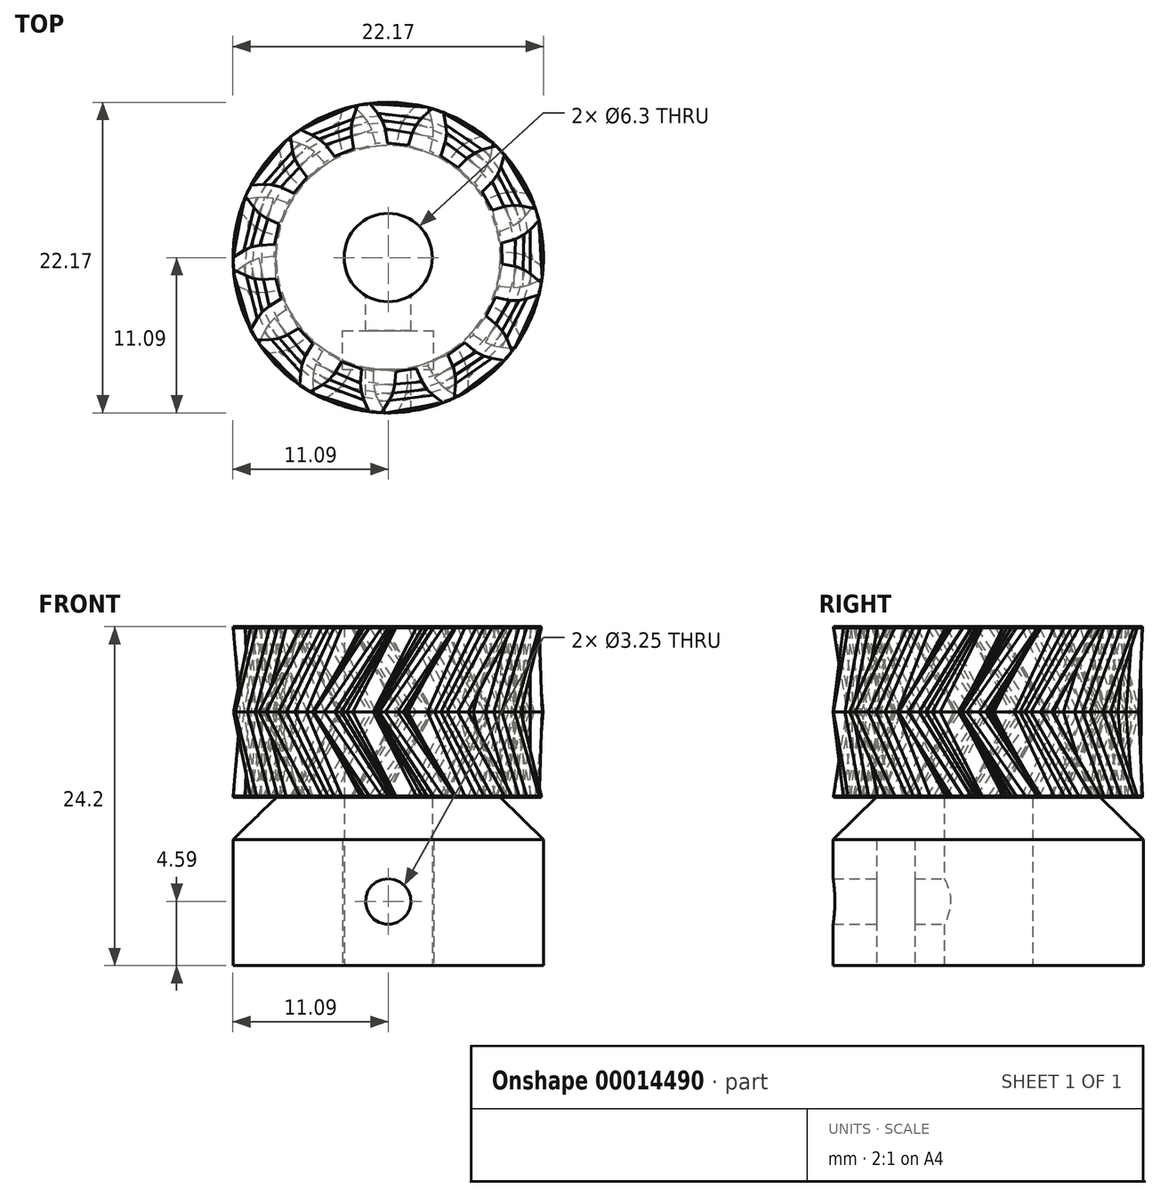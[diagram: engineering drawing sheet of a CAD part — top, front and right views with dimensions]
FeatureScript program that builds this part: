
annotation { "Feature Type Name" : "Feature", "Feature Type Description" : "" }
export const myFeature = defineFeature(function(context is Context, id is Id, definition is map)
    precondition{}
    {
        {
            var Q0;
            Q0=qCreatedBy(makeId("Top.planeOp"),FACE);
            cPlane(context, id + "F0", {"entities" : qUnion([Q0]), "cplaneType" : CPlaneType.OFFSET, "offset" : 6 * mm, "width" : 150 * mm, "height" : 150 * mm});
        }
        {
            var Q0;
            Q0=qCreatedBy(makeId("Top.planeOp"),FACE);
            var sketch = newSketch(context, id + "F1", { "sketchPlane" : qUnion([Q0])});
            skLineSegment(sketch, "E0", {"start": v(-2.62, 9.44) * mm, "end": v(-2.49, 10) * mm});
            skLineSegment(sketch, "E1", {"start": v(-2.49, 10) * mm, "end": v(-2.18, 10.87) * mm});
            skLineSegment(sketch, "E2", {"start": v(-1.33, 11) * mm, "end": v(-2.18, 10.87) * mm});
            skPoint(sketch, "E3.center", {"position": v(0, 0) * mm});
            skLineSegment(sketch, "E4", {"start": v(-1.76, 10.94) * mm, "end": v(-1.26, 7.98) * mm, "construction": true});
            skLineSegment(sketch, "E5", {"start": v(-2.47, 7.78) * mm, "end": v(-2.64, 8.79) * mm});
            skLineSegment(sketch, "E6", {"start": v(-2.64, 8.79) * mm, "end": v(-2.62, 9.44) * mm});
            skLineSegment(sketch, "E7.MirrorCS", {"start": v(-0.05, 8.18) * mm, "end": v(-0.22, 9.2) * mm});
            skLineSegment(sketch, "E8.MirrorCS", {"start": v(-0.22, 9.2) * mm, "end": v(-0.45, 9.8) * mm});
            skLineSegment(sketch, "E9.MirrorCS", {"start": v(-0.76, 10.3) * mm, "end": v(-1.33, 11) * mm});
            skLineSegment(sketch, "E10.MirrorCS", {"start": v(-0.45, 9.8) * mm, "end": v(-0.76, 10.3) * mm});
            skLineSegment(sketch, "E11", {"start": v(-0.05, 8.18) * mm, "end": v(1.43, 8.03) * mm});
            skLineSegment(sketch, "E12.1.0", {"start": v(-6.7, 7.14) * mm, "end": v(-6.85, 7.7) * mm});
            skLineSegment(sketch, "E12.1.1", {"start": v(-5.45, 8.76) * mm, "end": v(-6.3, 9.13) * mm});
            skLineSegment(sketch, "E12.1.2", {"start": v(-6.3, 9.13) * mm, "end": v(-6.98, 8.6) * mm});
            skLineSegment(sketch, "E12.1.3", {"start": v(-6.85, 7.7) * mm, "end": v(-6.98, 8.6) * mm});
            skLineSegment(sketch, "E12.1.4", {"start": v(-5.8, 5.74) * mm, "end": v(-6.42, 6.55) * mm});
            skLineSegment(sketch, "E12.1.5", {"start": v(-4.47, 8.04) * mm, "end": v(-4.96, 8.47) * mm});
            skLineSegment(sketch, "E12.1.6", {"start": v(-3.85, 7.22) * mm, "end": v(-2.47, 7.78) * mm});
            skLineSegment(sketch, "E12.1.7", {"start": v(-4.96, 8.47) * mm, "end": v(-5.45, 8.76) * mm});
            skLineSegment(sketch, "E12.1.8", {"start": v(-6.42, 6.55) * mm, "end": v(-6.7, 7.14) * mm});
            skLineSegment(sketch, "E12.1.9", {"start": v(-3.85, 7.22) * mm, "end": v(-4.47, 8.04) * mm});
            skLineSegment(sketch, "E12.2.0", {"start": v(-9.26, 3.2) * mm, "end": v(-9.64, 3.63) * mm});
            skLineSegment(sketch, "E12.2.1", {"start": v(-8.9, 5.22) * mm, "end": v(-9.81, 5.16) * mm});
            skLineSegment(sketch, "E12.2.2", {"start": v(-9.81, 5.16) * mm, "end": v(-10.18, 4.38) * mm});
            skLineSegment(sketch, "E12.2.3", {"start": v(-9.64, 3.63) * mm, "end": v(-10.18, 4.38) * mm});
            skLineSegment(sketch, "E12.2.4", {"start": v(-7.8, 2.39) * mm, "end": v(-8.73, 2.82) * mm});
            skLineSegment(sketch, "E12.2.5", {"start": v(-7.69, 5.04) * mm, "end": v(-8.33, 5.2) * mm});
            skLineSegment(sketch, "E12.2.6", {"start": v(-6.76, 4.6) * mm, "end": v(-5.8, 5.74) * mm});
            skLineSegment(sketch, "E12.2.7", {"start": v(-8.33, 5.2) * mm, "end": v(-8.9, 5.22) * mm});
            skLineSegment(sketch, "E12.2.8", {"start": v(-8.73, 2.82) * mm, "end": v(-9.26, 3.2) * mm});
            skLineSegment(sketch, "E12.2.9", {"start": v(-6.76, 4.6) * mm, "end": v(-7.69, 5.04) * mm});
            skLineSegment(sketch, "E12.3.0", {"start": v(-9.7, -1.46) * mm, "end": v(-10.23, -1.26) * mm});
            skLineSegment(sketch, "E12.3.1", {"start": v(-10.3, 0.49) * mm, "end": v(-11.09, 0) * mm});
            skLineSegment(sketch, "E12.3.2", {"start": v(-11.09, 0) * mm, "end": v(-11.05, -0.86) * mm});
            skLineSegment(sketch, "E12.3.3", {"start": v(-10.23, -1.26) * mm, "end": v(-11.05, -0.86) * mm});
            skLineSegment(sketch, "E12.3.4", {"start": v(-8.02, -1.51) * mm, "end": v(-9.04, -1.56) * mm});
            skLineSegment(sketch, "E12.3.5", {"start": v(-9.15, 0.89) * mm, "end": v(-9.8, 0.73) * mm});
            skLineSegment(sketch, "E12.3.6", {"start": v(-8.13, 0.94) * mm, "end": v(-7.8, 2.39) * mm});
            skLineSegment(sketch, "E12.3.7", {"start": v(-9.8, 0.73) * mm, "end": v(-10.3, 0.49) * mm});
            skLineSegment(sketch, "E12.3.8", {"start": v(-9.04, -1.56) * mm, "end": v(-9.7, -1.46) * mm});
            skLineSegment(sketch, "E12.3.9", {"start": v(-8.13, 0.94) * mm, "end": v(-9.15, 0.89) * mm});
            skLineSegment(sketch, "E12.4.0", {"start": v(-7.9, -5.8) * mm, "end": v(-8.47, -5.87) * mm});
            skLineSegment(sketch, "E12.4.1", {"start": v(-9.35, -4.36) * mm, "end": v(-9.82, -5.15) * mm});
            skLineSegment(sketch, "E12.4.2", {"start": v(-9.82, -5.15) * mm, "end": v(-9.39, -5.9) * mm});
            skLineSegment(sketch, "E12.4.3", {"start": v(-8.47, -5.87) * mm, "end": v(-9.39, -5.9) * mm});
            skLineSegment(sketch, "E12.4.4", {"start": v(-6.4, -5.06) * mm, "end": v(-7.28, -5.58) * mm});
            skLineSegment(sketch, "E12.4.5", {"start": v(-8.52, -3.47) * mm, "end": v(-9.01, -3.9) * mm});
            skLineSegment(sketch, "E12.4.6", {"start": v(-7.63, -2.95) * mm, "end": v(-8.02, -1.51) * mm});
            skLineSegment(sketch, "E12.4.7", {"start": v(-9.01, -3.9) * mm, "end": v(-9.35, -4.36) * mm});
            skLineSegment(sketch, "E12.4.8", {"start": v(-7.28, -5.58) * mm, "end": v(-7.9, -5.8) * mm});
            skLineSegment(sketch, "E12.4.9", {"start": v(-7.63, -2.95) * mm, "end": v(-8.52, -3.47) * mm});
            skLineSegment(sketch, "E12.5.0", {"start": v(-4.3, -8.8) * mm, "end": v(-4.77, -9.13) * mm});
            skLineSegment(sketch, "E12.5.1", {"start": v(-6.26, -8.2) * mm, "end": v(-6.3, -9.12) * mm});
            skLineSegment(sketch, "E12.5.2", {"start": v(-6.3, -9.12) * mm, "end": v(-5.57, -9.58) * mm});
            skLineSegment(sketch, "E12.5.3", {"start": v(-4.77, -9.13) * mm, "end": v(-5.57, -9.58) * mm});
            skLineSegment(sketch, "E12.5.4", {"start": v(-3.3, -7.46) * mm, "end": v(-3.85, -8.32) * mm});
            skLineSegment(sketch, "E12.5.5", {"start": v(-5.93, -7.03) * mm, "end": v(-6.17, -7.64) * mm});
            skLineSegment(sketch, "E12.5.6", {"start": v(-5.39, -6.16) * mm, "end": v(-6.4, -5.06) * mm});
            skLineSegment(sketch, "E12.5.7", {"start": v(-6.17, -7.64) * mm, "end": v(-6.26, -8.2) * mm});
            skLineSegment(sketch, "E12.5.8", {"start": v(-3.85, -8.32) * mm, "end": v(-4.3, -8.8) * mm});
            skLineSegment(sketch, "E12.5.9", {"start": v(-5.39, -6.16) * mm, "end": v(-5.93, -7.03) * mm});
            skLineSegment(sketch, "E12.6.0", {"start": v(0.28, -9.8) * mm, "end": v(0.02, -10.3) * mm});
            skLineSegment(sketch, "E12.6.1", {"start": v(-1.73, -10.17) * mm, "end": v(-1.34, -11) * mm});
            skLineSegment(sketch, "E12.6.2", {"start": v(-1.34, -11) * mm, "end": v(-0.48, -11.07) * mm});
            skLineSegment(sketch, "E12.6.3", {"start": v(0.02, -10.3) * mm, "end": v(-0.48, -11.07) * mm});
            skLineSegment(sketch, "E12.6.4", {"start": v(0.53, -8.14) * mm, "end": v(0.46, -9.16) * mm});
            skLineSegment(sketch, "E12.6.5", {"start": v(-1.99, -8.98) * mm, "end": v(-1.9, -9.63) * mm});
            skLineSegment(sketch, "E12.6.6", {"start": v(-1.9, -7.96) * mm, "end": v(-3.3, -7.46) * mm});
            skLineSegment(sketch, "E12.6.7", {"start": v(-1.9, -9.63) * mm, "end": v(-1.73, -10.17) * mm});
            skLineSegment(sketch, "E12.6.8", {"start": v(0.46, -9.16) * mm, "end": v(0.28, -9.8) * mm});
            skLineSegment(sketch, "E12.6.9", {"start": v(-1.9, -7.96) * mm, "end": v(-1.99, -8.98) * mm});
            skLineSegment(sketch, "E12.7.0", {"start": v(4.8, -8.54) * mm, "end": v(4.8, -9.11) * mm});
            skLineSegment(sketch, "E12.7.1", {"start": v(3.2, -9.8) * mm, "end": v(3.92, -10.37) * mm});
            skLineSegment(sketch, "E12.7.2", {"start": v(3.92, -10.37) * mm, "end": v(4.72, -10.03) * mm});
            skLineSegment(sketch, "E12.7.3", {"start": v(4.8, -9.11) * mm, "end": v(4.72, -10.03) * mm});
            skLineSegment(sketch, "E12.7.4", {"start": v(4.26, -6.96) * mm, "end": v(4.66, -7.9) * mm});
            skLineSegment(sketch, "E12.7.5", {"start": v(2.41, -8.87) * mm, "end": v(2.79, -9.41) * mm});
            skLineSegment(sketch, "E12.7.6", {"start": v(2, -7.93) * mm, "end": v(0.53, -8.14) * mm});
            skLineSegment(sketch, "E12.7.7", {"start": v(2.79, -9.41) * mm, "end": v(3.2, -9.8) * mm});
            skLineSegment(sketch, "E12.7.8", {"start": v(4.66, -7.9) * mm, "end": v(4.8, -8.54) * mm});
            skLineSegment(sketch, "E12.7.9", {"start": v(2, -7.93) * mm, "end": v(2.41, -8.87) * mm});
            skLineSegment(sketch, "E12.8.0", {"start": v(8.22, -5.33) * mm, "end": v(8.5, -5.84) * mm});
            skLineSegment(sketch, "E12.8.1", {"start": v(7.4, -7.2) * mm, "end": v(8.3, -7.36) * mm});
            skLineSegment(sketch, "E12.8.2", {"start": v(8.3, -7.36) * mm, "end": v(8.84, -6.69) * mm});
            skLineSegment(sketch, "E12.8.3", {"start": v(8.5, -5.84) * mm, "end": v(8.84, -6.69) * mm});
            skLineSegment(sketch, "E12.8.4", {"start": v(7, -4.18) * mm, "end": v(7.8, -4.83) * mm});
            skLineSegment(sketch, "E12.8.5", {"start": v(6.26, -6.73) * mm, "end": v(6.84, -7.04) * mm});
            skLineSegment(sketch, "E12.8.6", {"start": v(5.46, -6.09) * mm, "end": v(4.26, -6.96) * mm});
            skLineSegment(sketch, "E12.8.7", {"start": v(6.84, -7.04) * mm, "end": v(7.4, -7.2) * mm});
            skLineSegment(sketch, "E12.8.8", {"start": v(7.8, -4.83) * mm, "end": v(8.22, -5.33) * mm});
            skLineSegment(sketch, "E12.8.9", {"start": v(5.46, -6.09) * mm, "end": v(6.26, -6.73) * mm});
            skLineSegment(sketch, "E12.9.0", {"start": v(9.76, -0.9) * mm, "end": v(10.23, -1.22) * mm});
            skLineSegment(sketch, "E12.9.1", {"start": v(9.9, -2.94) * mm, "end": v(10.76, -2.66) * mm});
            skLineSegment(sketch, "E12.9.2", {"start": v(10.76, -2.66) * mm, "end": v(10.93, -1.81) * mm});
            skLineSegment(sketch, "E12.9.3", {"start": v(10.23, -1.22) * mm, "end": v(10.93, -1.81) * mm});
            skLineSegment(sketch, "E12.9.4", {"start": v(8.15, -0.45) * mm, "end": v(9.15, -0.65) * mm});
            skLineSegment(sketch, "E12.9.5", {"start": v(8.67, -3.05) * mm, "end": v(9.33, -3.06) * mm});
            skLineSegment(sketch, "E12.9.6", {"start": v(7.67, -2.85) * mm, "end": v(7, -4.18) * mm});
            skLineSegment(sketch, "E12.9.7", {"start": v(9.33, -3.06) * mm, "end": v(9.9, -2.94) * mm});
            skLineSegment(sketch, "E12.9.8", {"start": v(9.15, -0.65) * mm, "end": v(9.76, -0.9) * mm});
            skLineSegment(sketch, "E12.9.9", {"start": v(7.67, -2.85) * mm, "end": v(8.67, -3.05) * mm});
            skLineSegment(sketch, "E12.10.0", {"start": v(9.06, 3.74) * mm, "end": v(9.63, 3.67) * mm});
            skLineSegment(sketch, "E12.10.1", {"start": v(10.12, 2) * mm, "end": v(10.77, 2.65) * mm});
            skLineSegment(sketch, "E12.10.2", {"start": v(10.77, 2.65) * mm, "end": v(10.52, 3.48) * mm});
            skLineSegment(sketch, "E12.10.3", {"start": v(9.63, 3.67) * mm, "end": v(10.52, 3.48) * mm});
            skLineSegment(sketch, "E12.10.4", {"start": v(7.42, 3.39) * mm, "end": v(8.4, 3.68) * mm});
            skLineSegment(sketch, "E12.10.5", {"start": v(9.1, 1.33) * mm, "end": v(9.68, 1.63) * mm});
            skLineSegment(sketch, "E12.10.6", {"start": v(8.11, 1.04) * mm, "end": v(8.15, -0.45) * mm});
            skLineSegment(sketch, "E12.10.7", {"start": v(9.68, 1.63) * mm, "end": v(10.12, 2) * mm});
            skLineSegment(sketch, "E12.10.8", {"start": v(8.4, 3.68) * mm, "end": v(9.06, 3.74) * mm});
            skLineSegment(sketch, "E12.10.9", {"start": v(8.11, 1.04) * mm, "end": v(9.1, 1.33) * mm});
            skLineSegment(sketch, "E12.11.0", {"start": v(6.28, 7.52) * mm, "end": v(6.82, 7.73) * mm});
            skLineSegment(sketch, "E12.11.1", {"start": v(8.04, 6.47) * mm, "end": v(8.3, 7.35) * mm});
            skLineSegment(sketch, "E12.11.2", {"start": v(8.3, 7.35) * mm, "end": v(7.7, 7.97) * mm});
            skLineSegment(sketch, "E12.11.3", {"start": v(6.82, 7.73) * mm, "end": v(7.7, 7.97) * mm});
            skLineSegment(sketch, "E12.11.4", {"start": v(5, 6.45) * mm, "end": v(5.73, 7.16) * mm});
            skLineSegment(sketch, "E12.11.5", {"start": v(7.44, 5.4) * mm, "end": v(7.82, 5.94) * mm});
            skLineSegment(sketch, "E12.11.6", {"start": v(6.7, 4.69) * mm, "end": v(7.42, 3.39) * mm});
            skLineSegment(sketch, "E12.11.7", {"start": v(7.82, 5.94) * mm, "end": v(8.04, 6.47) * mm});
            skLineSegment(sketch, "E12.11.8", {"start": v(5.73, 7.16) * mm, "end": v(6.28, 7.52) * mm});
            skLineSegment(sketch, "E12.11.9", {"start": v(6.7, 4.69) * mm, "end": v(7.44, 5.4) * mm});
            skLineSegment(sketch, "E12.12.0", {"start": v(2.07, 9.58) * mm, "end": v(2.45, 10.01) * mm});
            skLineSegment(sketch, "E12.12.1", {"start": v(4.11, 9.46) * mm, "end": v(3.94, 10.36) * mm});
            skLineSegment(sketch, "E12.12.2", {"start": v(3.94, 10.36) * mm, "end": v(3.12, 10.63) * mm});
            skLineSegment(sketch, "E12.12.3", {"start": v(2.45, 10.01) * mm, "end": v(3.12, 10.63) * mm});
            skLineSegment(sketch, "E12.12.4", {"start": v(1.43, 8.03) * mm, "end": v(1.75, 9) * mm});
            skLineSegment(sketch, "E12.12.5", {"start": v(4.08, 8.24) * mm, "end": v(4.16, 8.9) * mm});
            skLineSegment(sketch, "E12.12.6", {"start": v(3.76, 7.27) * mm, "end": v(5, 6.45) * mm});
            skLineSegment(sketch, "E12.12.7", {"start": v(4.16, 8.9) * mm, "end": v(4.11, 9.46) * mm});
            skLineSegment(sketch, "E12.12.8", {"start": v(1.75, 9) * mm, "end": v(2.07, 9.58) * mm});
            skLineSegment(sketch, "E12.12.9", {"start": v(3.76, 7.27) * mm, "end": v(4.08, 8.24) * mm});
            skSolve(sketch);
        }
        {
            var Q0;
            Q0 = qSketchRegion(id + "F1", true);
            extrude(context, id + "F2", {"entities" : qUnion([Q0]), "oppositeDirection" : true, "depth" : .1 * mm});
        }
        {
            var Q0;
            Q0=qCreatedBy(id+"F0.planeOp",FACE);
            var sketch = newSketch(context, id + "F3", { "sketchPlane" : qUnion([Q0])});
            skLineSegment(sketch, "E13.0.0", {"start": v(1.4, 10.2) * mm, "end": v(1.07, 9.74) * mm});
            skLineSegment(sketch, "E13.0.1", {"start": v(1.07, 9.74) * mm, "end": v(0.81, 9.14) * mm});
            skLineSegment(sketch, "E13.0.2", {"start": v(0.81, 9.14) * mm, "end": v(0.6, 8.14) * mm});
            skLineSegment(sketch, "E13.0.3", {"start": v(0.6, 8.14) * mm, "end": v(-0.9, 8.13) * mm});
            skLineSegment(sketch, "E13.0.4", {"start": v(-0.9, 8.13) * mm, "end": v(-1.17, 9.12) * mm});
            skLineSegment(sketch, "E13.0.5", {"start": v(-1.17, 9.12) * mm, "end": v(-1.46, 9.7) * mm});
            skLineSegment(sketch, "E13.0.6", {"start": v(-1.46, 9.7) * mm, "end": v(-1.82, 10.16) * mm});
            skLineSegment(sketch, "E13.0.7", {"start": v(-1.82, 10.16) * mm, "end": v(-2.46, 10.81) * mm});
            skLineSegment(sketch, "E13.0.8", {"start": v(-2.46, 10.81) * mm, "end": v(-3.3, 10.58) * mm});
            skLineSegment(sketch, "E13.0.9", {"start": v(-3.3, 10.58) * mm, "end": v(-3.5, 9.7) * mm});
            skLineSegment(sketch, "E13.0.10", {"start": v(-3.5, 9.7) * mm, "end": v(-3.58, 9.12) * mm});
            skLineSegment(sketch, "E13.0.11", {"start": v(-3.58, 9.12) * mm, "end": v(-3.53, 8.47) * mm});
            skLineSegment(sketch, "E13.0.12", {"start": v(-3.53, 8.47) * mm, "end": v(-3.26, 7.48) * mm});
            skLineSegment(sketch, "E13.0.13", {"start": v(-3.26, 7.48) * mm, "end": v(-4.57, 6.78) * mm});
            skLineSegment(sketch, "E13.0.14", {"start": v(-4.57, 6.78) * mm, "end": v(-5.27, 7.53) * mm});
            skLineSegment(sketch, "E13.0.15", {"start": v(-5.27, 7.53) * mm, "end": v(-5.8, 7.92) * mm});
            skLineSegment(sketch, "E13.0.16", {"start": v(-5.8, 7.92) * mm, "end": v(-6.33, 8.15) * mm});
            skLineSegment(sketch, "E13.0.17", {"start": v(-6.33, 8.15) * mm, "end": v(-7.2, 8.43) * mm});
            skLineSegment(sketch, "E13.0.18", {"start": v(-7.2, 8.43) * mm, "end": v(-7.83, 7.84) * mm});
            skLineSegment(sketch, "E13.0.19", {"start": v(-7.83, 7.84) * mm, "end": v(-7.6, 6.95) * mm});
            skLineSegment(sketch, "E13.0.20", {"start": v(-7.6, 6.95) * mm, "end": v(-7.4, 6.41) * mm});
            skLineSegment(sketch, "E13.0.21", {"start": v(-7.4, 6.41) * mm, "end": v(-7.06, 5.86) * mm});
            skLineSegment(sketch, "E13.0.22", {"start": v(-7.06, 5.86) * mm, "end": v(-6.36, 5.1) * mm});
            skLineSegment(sketch, "E13.0.23", {"start": v(-6.36, 5.1) * mm, "end": v(-7.2, 3.88) * mm});
            skLineSegment(sketch, "E13.0.24", {"start": v(-7.2, 3.88) * mm, "end": v(-8.17, 4.22) * mm});
            skLineSegment(sketch, "E13.0.25", {"start": v(-8.17, 4.22) * mm, "end": v(-8.82, 4.31) * mm});
            skLineSegment(sketch, "E13.0.26", {"start": v(-8.82, 4.31) * mm, "end": v(-9.4, 4.28) * mm});
            skLineSegment(sketch, "E13.0.27", {"start": v(-9.4, 4.28) * mm, "end": v(-10.3, 4.12) * mm});
            skLineSegment(sketch, "E13.0.28", {"start": v(-10.3, 4.12) * mm, "end": v(-10.58, 3.3) * mm});
            skLineSegment(sketch, "E13.0.29", {"start": v(-10.58, 3.3) * mm, "end": v(-9.97, 2.62) * mm});
            skLineSegment(sketch, "E13.0.30", {"start": v(-9.97, 2.62) * mm, "end": v(-9.54, 2.24) * mm});
            skLineSegment(sketch, "E13.0.31", {"start": v(-9.54, 2.24) * mm, "end": v(-8.97, 1.9) * mm});
            skLineSegment(sketch, "E13.0.32", {"start": v(-8.97, 1.9) * mm, "end": v(-8, 1.57) * mm});
            skLineSegment(sketch, "E13.0.33", {"start": v(-8, 1.57) * mm, "end": v(-8.18, 0.1) * mm});
            skLineSegment(sketch, "E13.0.34", {"start": v(-8.18, 0.1) * mm, "end": v(-9.2, -0.06) * mm});
            skLineSegment(sketch, "E13.0.35", {"start": v(-9.2, -0.06) * mm, "end": v(-9.81, -0.28) * mm});
            skLineSegment(sketch, "E13.0.36", {"start": v(-9.81, -0.28) * mm, "end": v(-10.3, -0.58) * mm});
            skLineSegment(sketch, "E13.0.37", {"start": v(-10.3, -0.58) * mm, "end": v(-11.03, -1.14) * mm});
            skLineSegment(sketch, "E13.0.38", {"start": v(-11.03, -1.14) * mm, "end": v(-10.9, -2) * mm});
            skLineSegment(sketch, "E13.0.39", {"start": v(-10.9, -2) * mm, "end": v(-10.04, -2.31) * mm});
            skLineSegment(sketch, "E13.0.40", {"start": v(-10.04, -2.31) * mm, "end": v(-9.49, -2.45) * mm});
            skLineSegment(sketch, "E13.0.41", {"start": v(-9.49, -2.45) * mm, "end": v(-8.83, -2.48) * mm});
            skLineSegment(sketch, "E13.0.42", {"start": v(-8.83, -2.48) * mm, "end": v(-7.82, -2.33) * mm});
            skLineSegment(sketch, "E13.0.43", {"start": v(-7.82, -2.33) * mm, "end": v(-7.29, -3.72) * mm});
            skLineSegment(sketch, "E13.0.44", {"start": v(-7.29, -3.72) * mm, "end": v(-8.11, -4.33) * mm});
            skLineSegment(sketch, "E13.0.45", {"start": v(-8.11, -4.33) * mm, "end": v(-8.56, -4.8) * mm});
            skLineSegment(sketch, "E13.0.46", {"start": v(-8.56, -4.8) * mm, "end": v(-8.85, -5.3) * mm});
            skLineSegment(sketch, "E13.0.47", {"start": v(-8.85, -5.3) * mm, "end": v(-9.24, -6.13) * mm});
            skLineSegment(sketch, "E13.0.48", {"start": v(-9.24, -6.13) * mm, "end": v(-8.73, -6.83) * mm});
            skLineSegment(sketch, "E13.0.49", {"start": v(-8.73, -6.83) * mm, "end": v(-7.82, -6.71) * mm});
            skLineSegment(sketch, "E13.0.50", {"start": v(-7.82, -6.71) * mm, "end": v(-7.26, -6.58) * mm});
            skLineSegment(sketch, "E13.0.51", {"start": v(-7.26, -6.58) * mm, "end": v(-6.67, -6.3) * mm});
            skLineSegment(sketch, "E13.0.52", {"start": v(-6.67, -6.3) * mm, "end": v(-5.84, -5.7) * mm});
            skLineSegment(sketch, "E13.0.53", {"start": v(-5.84, -5.7) * mm, "end": v(-4.72, -6.68) * mm});
            skLineSegment(sketch, "E13.0.54", {"start": v(-4.72, -6.68) * mm, "end": v(-5.17, -7.6) * mm});
            skLineSegment(sketch, "E13.0.55", {"start": v(-5.17, -7.6) * mm, "end": v(-5.35, -8.24) * mm});
            skLineSegment(sketch, "E13.0.56", {"start": v(-5.35, -8.24) * mm, "end": v(-5.38, -8.8) * mm});
            skLineSegment(sketch, "E13.0.57", {"start": v(-5.38, -8.8) * mm, "end": v(-5.33, -9.72) * mm});
            skLineSegment(sketch, "E13.0.58", {"start": v(-5.33, -9.72) * mm, "end": v(-4.55, -10.1) * mm});
            skLineSegment(sketch, "E13.0.59", {"start": v(-4.55, -10.1) * mm, "end": v(-3.8, -9.58) * mm});
            skLineSegment(sketch, "E13.0.60", {"start": v(-3.8, -9.58) * mm, "end": v(-3.37, -9.2) * mm});
            skLineSegment(sketch, "E13.0.61", {"start": v(-3.37, -9.2) * mm, "end": v(-2.97, -8.68) * mm});
            skLineSegment(sketch, "E13.0.62", {"start": v(-2.97, -8.68) * mm, "end": v(-2.52, -7.76) * mm});
            skLineSegment(sketch, "E13.0.63", {"start": v(-2.52, -7.76) * mm, "end": v(-1.08, -8.1) * mm});
            skLineSegment(sketch, "E13.0.64", {"start": v(-1.08, -8.1) * mm, "end": v(-1.05, -9.13) * mm});
            skLineSegment(sketch, "E13.0.65", {"start": v(-1.05, -9.13) * mm, "end": v(-0.9, -9.78) * mm});
            skLineSegment(sketch, "E13.0.66", {"start": v(-0.9, -9.78) * mm, "end": v(-0.67, -10.3) * mm});
            skLineSegment(sketch, "E13.0.67", {"start": v(-0.67, -10.3) * mm, "end": v(-0.2, -11.09) * mm});
            skLineSegment(sketch, "E13.0.68", {"start": v(-0.2, -11.09) * mm, "end": v(0.66, -11.06) * mm});
            skLineSegment(sketch, "E13.0.69", {"start": v(0.66, -11.06) * mm, "end": v(1.08, -10.25) * mm});
            skLineSegment(sketch, "E13.0.70", {"start": v(1.08, -10.25) * mm, "end": v(1.3, -9.71) * mm});
            skLineSegment(sketch, "E13.0.71", {"start": v(1.3, -9.71) * mm, "end": v(1.4, -9.07) * mm});
            skLineSegment(sketch, "E13.0.72", {"start": v(1.4, -9.07) * mm, "end": v(1.37, -8.04) * mm});
            skLineSegment(sketch, "E13.0.73", {"start": v(1.37, -8.04) * mm, "end": v(2.81, -7.68) * mm});
            skLineSegment(sketch, "E13.0.74", {"start": v(2.81, -7.68) * mm, "end": v(3.32, -8.58) * mm});
            skLineSegment(sketch, "E13.0.75", {"start": v(3.32, -8.58) * mm, "end": v(3.74, -9.08) * mm});
            skLineSegment(sketch, "E13.0.76", {"start": v(3.74, -9.08) * mm, "end": v(4.2, -9.43) * mm});
            skLineSegment(sketch, "E13.0.77", {"start": v(4.2, -9.43) * mm, "end": v(4.97, -9.91) * mm});
            skLineSegment(sketch, "E13.0.78", {"start": v(4.97, -9.91) * mm, "end": v(5.73, -9.49) * mm});
            skLineSegment(sketch, "E13.0.79", {"start": v(5.73, -9.49) * mm, "end": v(5.72, -8.57) * mm});
            skLineSegment(sketch, "E13.0.80", {"start": v(5.72, -8.57) * mm, "end": v(5.66, -8) * mm});
            skLineSegment(sketch, "E13.0.81", {"start": v(5.66, -8) * mm, "end": v(5.45, -7.38) * mm});
            skLineSegment(sketch, "E13.0.82", {"start": v(5.45, -7.38) * mm, "end": v(4.95, -6.48) * mm});
            skLineSegment(sketch, "E13.0.83", {"start": v(4.95, -6.48) * mm, "end": v(6.06, -5.5) * mm});
            skLineSegment(sketch, "E13.0.84", {"start": v(6.06, -5.5) * mm, "end": v(6.92, -6.05) * mm});
            skLineSegment(sketch, "E13.0.85", {"start": v(6.92, -6.05) * mm, "end": v(7.53, -6.3) * mm});
            skLineSegment(sketch, "E13.0.86", {"start": v(7.53, -6.3) * mm, "end": v(8.1, -6.4) * mm});
            skLineSegment(sketch, "E13.0.87", {"start": v(8.1, -6.4) * mm, "end": v(9, -6.46) * mm});
            skLineSegment(sketch, "E13.0.88", {"start": v(9, -6.46) * mm, "end": v(9.48, -5.74) * mm});
            skLineSegment(sketch, "E13.0.89", {"start": v(9.48, -5.74) * mm, "end": v(9.05, -4.93) * mm});
            skLineSegment(sketch, "E13.0.90", {"start": v(9.05, -4.93) * mm, "end": v(8.73, -4.46) * mm});
            skLineSegment(sketch, "E13.0.91", {"start": v(8.73, -4.46) * mm, "end": v(8.26, -4) * mm});
            skLineSegment(sketch, "E13.0.92", {"start": v(8.26, -4) * mm, "end": v(7.4, -3.44) * mm});
            skLineSegment(sketch, "E13.0.93", {"start": v(7.4, -3.44) * mm, "end": v(7.92, -2.05) * mm});
            skLineSegment(sketch, "E13.0.94", {"start": v(7.92, -2.05) * mm, "end": v(8.94, -2.14) * mm});
            skLineSegment(sketch, "E13.0.95", {"start": v(8.94, -2.14) * mm, "end": v(9.6, -2.08) * mm});
            skLineSegment(sketch, "E13.0.96", {"start": v(9.6, -2.08) * mm, "end": v(10.14, -1.9) * mm});
            skLineSegment(sketch, "E13.0.97", {"start": v(10.14, -1.9) * mm, "end": v(10.98, -1.54) * mm});
            skLineSegment(sketch, "E13.0.98", {"start": v(10.98, -1.54) * mm, "end": v(11.06, -0.68) * mm});
            skLineSegment(sketch, "E13.0.99", {"start": v(11.06, -0.68) * mm, "end": v(10.3, -0.16) * mm});
            skLineSegment(sketch, "E13.0.100", {"start": v(10.3, -0.16) * mm, "end": v(9.8, 0.11) * mm});
            skLineSegment(sketch, "E13.0.101", {"start": v(9.8, 0.11) * mm, "end": v(9.17, 0.3) * mm});
            skLineSegment(sketch, "E13.0.102", {"start": v(9.17, 0.3) * mm, "end": v(8.15, 0.4) * mm});
            skLineSegment(sketch, "E13.0.103", {"start": v(8.15, 0.4) * mm, "end": v(7.96, 1.87) * mm});
            skLineSegment(sketch, "E13.0.104", {"start": v(7.96, 1.87) * mm, "end": v(8.91, 2.26) * mm});
            skLineSegment(sketch, "E13.0.105", {"start": v(8.91, 2.26) * mm, "end": v(9.46, 2.62) * mm});
            skLineSegment(sketch, "E13.0.106", {"start": v(9.46, 2.62) * mm, "end": v(9.86, 3.03) * mm});
            skLineSegment(sketch, "E13.0.107", {"start": v(9.86, 3.03) * mm, "end": v(10.44, 3.74) * mm});
            skLineSegment(sketch, "E13.0.108", {"start": v(10.44, 3.74) * mm, "end": v(10.1, 4.54) * mm});
            skLineSegment(sketch, "E13.0.109", {"start": v(10.1, 4.54) * mm, "end": v(9.2, 4.65) * mm});
            skLineSegment(sketch, "E13.0.110", {"start": v(9.2, 4.65) * mm, "end": v(8.63, 4.65) * mm});
            skLineSegment(sketch, "E13.0.111", {"start": v(8.63, 4.65) * mm, "end": v(7.98, 4.52) * mm});
            skLineSegment(sketch, "E13.0.112", {"start": v(7.98, 4.52) * mm, "end": v(7.03, 4.13) * mm});
            skLineSegment(sketch, "E13.0.113", {"start": v(7.03, 4.13) * mm, "end": v(6.18, 5.36) * mm});
            skLineSegment(sketch, "E13.0.114", {"start": v(6.18, 5.36) * mm, "end": v(6.84, 6.14) * mm});
            skLineSegment(sketch, "E13.0.115", {"start": v(6.84, 6.14) * mm, "end": v(7.16, 6.72) * mm});
            skLineSegment(sketch, "E13.0.116", {"start": v(7.16, 6.72) * mm, "end": v(7.33, 7.26) * mm});
            skLineSegment(sketch, "E13.0.117", {"start": v(7.33, 7.26) * mm, "end": v(7.5, 8.16) * mm});
            skLineSegment(sketch, "E13.0.118", {"start": v(7.5, 8.16) * mm, "end": v(6.84, 8.72) * mm});
            skLineSegment(sketch, "E13.0.119", {"start": v(6.84, 8.72) * mm, "end": v(5.98, 8.39) * mm});
            skLineSegment(sketch, "E13.0.120", {"start": v(5.98, 8.39) * mm, "end": v(5.47, 8.13) * mm});
            skLineSegment(sketch, "E13.0.121", {"start": v(5.47, 8.13) * mm, "end": v(4.96, 7.71) * mm});
            skLineSegment(sketch, "E13.0.122", {"start": v(4.96, 7.71) * mm, "end": v(4.3, 6.93) * mm});
            skLineSegment(sketch, "E13.0.123", {"start": v(4.3, 6.93) * mm, "end": v(2.99, 7.62) * mm});
            skLineSegment(sketch, "E13.0.124", {"start": v(2.99, 7.62) * mm, "end": v(3.2, 8.62) * mm});
            skLineSegment(sketch, "E13.0.125", {"start": v(3.2, 8.62) * mm, "end": v(3.22, 9.28) * mm});
            skLineSegment(sketch, "E13.0.126", {"start": v(3.22, 9.28) * mm, "end": v(3.11, 9.84) * mm});
            skLineSegment(sketch, "E13.0.127", {"start": v(3.11, 9.84) * mm, "end": v(2.85, 10.72) * mm});
            skLineSegment(sketch, "E13.0.128", {"start": v(2.85, 10.72) * mm, "end": v(2, 10.9) * mm});
            skLineSegment(sketch, "E13.0.129", {"start": v(2, 10.9) * mm, "end": v(1.4, 10.2) * mm});
            skLineSegment(sketch, "E14", {"start": v(0, 0) * mm, "end": v(2.8, 10.73) * mm, "construction": true});
            skSolve(sketch);
        }
        {
            var Q1;
            Q1 = qSketchRegion(id + "F1", true);
            var Q2;
            Q2 = qSketchRegion(id + "F3", true);
            var Q3;
            Q3=sQuery(id+"F1.wireOp",VERTEX,"E12.1.1.end");
            var Q4;
            Q4=sQuery(id+"F3.wireOp",VERTEX,"E13.0.7.end");
            loft(context, id + "F4", {"operationType" : NewBodyOperationType.ADD, "sheetProfilesArray" : [{ "sheetProfileEntities" : qUnion([Q1]) }, { "sheetProfileEntities" : qUnion([Q2]) }], "matchConnections" : true, "connections" : [{ "connectionEntities" : qUnion([Q3, Q4]), "connectionEdgeQueries" : qUnion([]), "connectionEdgeParameters" : [] }]});
        }
        {
            var Q0;
            Q0=makeQuery(id+"F2.opExtrude","SWEPT_BODY",BODY,{"disambiguationData":[OSD([sQuery(id+"F1.wireOp",EDGE,"E0"),sQuery(id+"F1.wireOp",EDGE,"E1"),sQuery(id+"F1.wireOp",EDGE,"E2"),sQuery(id+"F1.wireOp",EDGE,"E5"),sQuery(id+"F1.wireOp",EDGE,"E6"),sQuery(id+"F1.wireOp",EDGE,"E7.MirrorCS"),sQuery(id+"F1.wireOp",EDGE,"E8.MirrorCS"),sQuery(id+"F1.wireOp",EDGE,"E9.MirrorCS"),sQuery(id+"F1.wireOp",EDGE,"E10.MirrorCS"),sQuery(id+"F1.wireOp",EDGE,"E11"),sQuery(id+"F1.wireOp",EDGE,"E12.1.0"),sQuery(id+"F1.wireOp",EDGE,"E12.1.1"),sQuery(id+"F1.wireOp",EDGE,"E12.1.2"),sQuery(id+"F1.wireOp",EDGE,"E12.1.3"),sQuery(id+"F1.wireOp",EDGE,"E12.1.4"),sQuery(id+"F1.wireOp",EDGE,"E12.1.5"),sQuery(id+"F1.wireOp",EDGE,"E12.1.6"),sQuery(id+"F1.wireOp",EDGE,"E12.1.7"),sQuery(id+"F1.wireOp",EDGE,"E12.1.8"),sQuery(id+"F1.wireOp",EDGE,"E12.1.9"),sQuery(id+"F1.wireOp",EDGE,"E12.2.0"),sQuery(id+"F1.wireOp",EDGE,"E12.2.1"),sQuery(id+"F1.wireOp",EDGE,"E12.2.2"),sQuery(id+"F1.wireOp",EDGE,"E12.2.3"),sQuery(id+"F1.wireOp",EDGE,"E12.2.4"),sQuery(id+"F1.wireOp",EDGE,"E12.2.5"),sQuery(id+"F1.wireOp",EDGE,"E12.2.6"),sQuery(id+"F1.wireOp",EDGE,"E12.2.7"),sQuery(id+"F1.wireOp",EDGE,"E12.2.8"),sQuery(id+"F1.wireOp",EDGE,"E12.2.9"),sQuery(id+"F1.wireOp",EDGE,"E12.3.0"),sQuery(id+"F1.wireOp",EDGE,"E12.3.1"),sQuery(id+"F1.wireOp",EDGE,"E12.3.2"),sQuery(id+"F1.wireOp",EDGE,"E12.3.3"),sQuery(id+"F1.wireOp",EDGE,"E12.3.4"),sQuery(id+"F1.wireOp",EDGE,"E12.3.5"),sQuery(id+"F1.wireOp",EDGE,"E12.3.6"),sQuery(id+"F1.wireOp",EDGE,"E12.3.7"),sQuery(id+"F1.wireOp",EDGE,"E12.3.8"),sQuery(id+"F1.wireOp",EDGE,"E12.3.9"),sQuery(id+"F1.wireOp",EDGE,"E12.4.0"),sQuery(id+"F1.wireOp",EDGE,"E12.4.1"),sQuery(id+"F1.wireOp",EDGE,"E12.4.2"),sQuery(id+"F1.wireOp",EDGE,"E12.4.3"),sQuery(id+"F1.wireOp",EDGE,"E12.4.4"),sQuery(id+"F1.wireOp",EDGE,"E12.4.5"),sQuery(id+"F1.wireOp",EDGE,"E12.4.6"),sQuery(id+"F1.wireOp",EDGE,"E12.4.7"),sQuery(id+"F1.wireOp",EDGE,"E12.4.8"),sQuery(id+"F1.wireOp",EDGE,"E12.4.9"),sQuery(id+"F1.wireOp",EDGE,"E12.5.0"),sQuery(id+"F1.wireOp",EDGE,"E12.5.1"),sQuery(id+"F1.wireOp",EDGE,"E12.5.2"),sQuery(id+"F1.wireOp",EDGE,"E12.5.3"),sQuery(id+"F1.wireOp",EDGE,"E12.5.4"),sQuery(id+"F1.wireOp",EDGE,"E12.5.5"),sQuery(id+"F1.wireOp",EDGE,"E12.5.6"),sQuery(id+"F1.wireOp",EDGE,"E12.5.7"),sQuery(id+"F1.wireOp",EDGE,"E12.5.8"),sQuery(id+"F1.wireOp",EDGE,"E12.5.9"),sQuery(id+"F1.wireOp",EDGE,"E12.6.0"),sQuery(id+"F1.wireOp",EDGE,"E12.6.1"),sQuery(id+"F1.wireOp",EDGE,"E12.6.2"),sQuery(id+"F1.wireOp",EDGE,"E12.6.3"),sQuery(id+"F1.wireOp",EDGE,"E12.6.4"),sQuery(id+"F1.wireOp",EDGE,"E12.6.5"),sQuery(id+"F1.wireOp",EDGE,"E12.6.6"),sQuery(id+"F1.wireOp",EDGE,"E12.6.7"),sQuery(id+"F1.wireOp",EDGE,"E12.6.8"),sQuery(id+"F1.wireOp",EDGE,"E12.6.9"),sQuery(id+"F1.wireOp",EDGE,"E12.7.0"),sQuery(id+"F1.wireOp",EDGE,"E12.7.1"),sQuery(id+"F1.wireOp",EDGE,"E12.7.2"),sQuery(id+"F1.wireOp",EDGE,"E12.7.3"),sQuery(id+"F1.wireOp",EDGE,"E12.7.4"),sQuery(id+"F1.wireOp",EDGE,"E12.7.5"),sQuery(id+"F1.wireOp",EDGE,"E12.7.6"),sQuery(id+"F1.wireOp",EDGE,"E12.7.7"),sQuery(id+"F1.wireOp",EDGE,"E12.7.8"),sQuery(id+"F1.wireOp",EDGE,"E12.7.9"),sQuery(id+"F1.wireOp",EDGE,"E12.8.0"),sQuery(id+"F1.wireOp",EDGE,"E12.8.1"),sQuery(id+"F1.wireOp",EDGE,"E12.8.2"),sQuery(id+"F1.wireOp",EDGE,"E12.8.3"),sQuery(id+"F1.wireOp",EDGE,"E12.8.4"),sQuery(id+"F1.wireOp",EDGE,"E12.8.5"),sQuery(id+"F1.wireOp",EDGE,"E12.8.6"),sQuery(id+"F1.wireOp",EDGE,"E12.8.7"),sQuery(id+"F1.wireOp",EDGE,"E12.8.8"),sQuery(id+"F1.wireOp",EDGE,"E12.8.9"),sQuery(id+"F1.wireOp",EDGE,"E12.9.0"),sQuery(id+"F1.wireOp",EDGE,"E12.9.1"),sQuery(id+"F1.wireOp",EDGE,"E12.9.2"),sQuery(id+"F1.wireOp",EDGE,"E12.9.3"),sQuery(id+"F1.wireOp",EDGE,"E12.9.4"),sQuery(id+"F1.wireOp",EDGE,"E12.9.5"),sQuery(id+"F1.wireOp",EDGE,"E12.9.6"),sQuery(id+"F1.wireOp",EDGE,"E12.9.7"),sQuery(id+"F1.wireOp",EDGE,"E12.9.8"),sQuery(id+"F1.wireOp",EDGE,"E12.9.9"),sQuery(id+"F1.wireOp",EDGE,"E12.10.0"),sQuery(id+"F1.wireOp",EDGE,"E12.10.1"),sQuery(id+"F1.wireOp",EDGE,"E12.10.2"),sQuery(id+"F1.wireOp",EDGE,"E12.10.3"),sQuery(id+"F1.wireOp",EDGE,"E12.10.4"),sQuery(id+"F1.wireOp",EDGE,"E12.10.5"),sQuery(id+"F1.wireOp",EDGE,"E12.10.6"),sQuery(id+"F1.wireOp",EDGE,"E12.10.7"),sQuery(id+"F1.wireOp",EDGE,"E12.10.8"),sQuery(id+"F1.wireOp",EDGE,"E12.10.9"),sQuery(id+"F1.wireOp",EDGE,"E12.11.0"),sQuery(id+"F1.wireOp",EDGE,"E12.11.1"),sQuery(id+"F1.wireOp",EDGE,"E12.11.2"),sQuery(id+"F1.wireOp",EDGE,"E12.11.3"),sQuery(id+"F1.wireOp",EDGE,"E12.11.4"),sQuery(id+"F1.wireOp",EDGE,"E12.11.5"),sQuery(id+"F1.wireOp",EDGE,"E12.11.6"),sQuery(id+"F1.wireOp",EDGE,"E12.11.7"),sQuery(id+"F1.wireOp",EDGE,"E12.11.8"),sQuery(id+"F1.wireOp",EDGE,"E12.11.9"),sQuery(id+"F1.wireOp",EDGE,"E12.12.0"),sQuery(id+"F1.wireOp",EDGE,"E12.12.1"),sQuery(id+"F1.wireOp",EDGE,"E12.12.2"),sQuery(id+"F1.wireOp",EDGE,"E12.12.3"),sQuery(id+"F1.wireOp",EDGE,"E12.12.4"),sQuery(id+"F1.wireOp",EDGE,"E12.12.5"),sQuery(id+"F1.wireOp",EDGE,"E12.12.6"),sQuery(id+"F1.wireOp",EDGE,"E12.12.7"),sQuery(id+"F1.wireOp",EDGE,"E12.12.8"),sQuery(id+"F1.wireOp",EDGE,"E12.12.9")])]});
            var Q1;
            Q1=qCreatedBy(id+"F0.planeOp",FACE);
            mirror(context, id + "F5", {"operationType" : NewBodyOperationType.ADD, "entities" : qUnion([Q0]), "mirrorPlane" : qUnion([Q1])});
        }
        {
            var Q0;
            Q0=makeQuery(id+"F2.opExtrude","CAP_FACE",FACE,{"disambiguationData":[OSD([sQuery(id+"F1.wireOp",EDGE,"E0"),sQuery(id+"F1.wireOp",EDGE,"E1"),sQuery(id+"F1.wireOp",EDGE,"E2"),sQuery(id+"F1.wireOp",EDGE,"E5"),sQuery(id+"F1.wireOp",EDGE,"E6"),sQuery(id+"F1.wireOp",EDGE,"E7.MirrorCS"),sQuery(id+"F1.wireOp",EDGE,"E8.MirrorCS"),sQuery(id+"F1.wireOp",EDGE,"E9.MirrorCS"),sQuery(id+"F1.wireOp",EDGE,"E10.MirrorCS"),sQuery(id+"F1.wireOp",EDGE,"E11"),sQuery(id+"F1.wireOp",EDGE,"E12.1.0"),sQuery(id+"F1.wireOp",EDGE,"E12.1.1"),sQuery(id+"F1.wireOp",EDGE,"E12.1.2"),sQuery(id+"F1.wireOp",EDGE,"E12.1.3"),sQuery(id+"F1.wireOp",EDGE,"E12.1.4"),sQuery(id+"F1.wireOp",EDGE,"E12.1.5"),sQuery(id+"F1.wireOp",EDGE,"E12.1.6"),sQuery(id+"F1.wireOp",EDGE,"E12.1.7"),sQuery(id+"F1.wireOp",EDGE,"E12.1.8"),sQuery(id+"F1.wireOp",EDGE,"E12.1.9"),sQuery(id+"F1.wireOp",EDGE,"E12.2.0"),sQuery(id+"F1.wireOp",EDGE,"E12.2.1"),sQuery(id+"F1.wireOp",EDGE,"E12.2.2"),sQuery(id+"F1.wireOp",EDGE,"E12.2.3"),sQuery(id+"F1.wireOp",EDGE,"E12.2.4"),sQuery(id+"F1.wireOp",EDGE,"E12.2.5"),sQuery(id+"F1.wireOp",EDGE,"E12.2.6"),sQuery(id+"F1.wireOp",EDGE,"E12.2.7"),sQuery(id+"F1.wireOp",EDGE,"E12.2.8"),sQuery(id+"F1.wireOp",EDGE,"E12.2.9"),sQuery(id+"F1.wireOp",EDGE,"E12.3.0"),sQuery(id+"F1.wireOp",EDGE,"E12.3.1"),sQuery(id+"F1.wireOp",EDGE,"E12.3.2"),sQuery(id+"F1.wireOp",EDGE,"E12.3.3"),sQuery(id+"F1.wireOp",EDGE,"E12.3.4"),sQuery(id+"F1.wireOp",EDGE,"E12.3.5"),sQuery(id+"F1.wireOp",EDGE,"E12.3.6"),sQuery(id+"F1.wireOp",EDGE,"E12.3.7"),sQuery(id+"F1.wireOp",EDGE,"E12.3.8"),sQuery(id+"F1.wireOp",EDGE,"E12.3.9"),sQuery(id+"F1.wireOp",EDGE,"E12.4.0"),sQuery(id+"F1.wireOp",EDGE,"E12.4.1"),sQuery(id+"F1.wireOp",EDGE,"E12.4.2"),sQuery(id+"F1.wireOp",EDGE,"E12.4.3"),sQuery(id+"F1.wireOp",EDGE,"E12.4.4"),sQuery(id+"F1.wireOp",EDGE,"E12.4.5"),sQuery(id+"F1.wireOp",EDGE,"E12.4.6"),sQuery(id+"F1.wireOp",EDGE,"E12.4.7"),sQuery(id+"F1.wireOp",EDGE,"E12.4.8"),sQuery(id+"F1.wireOp",EDGE,"E12.4.9"),sQuery(id+"F1.wireOp",EDGE,"E12.5.0"),sQuery(id+"F1.wireOp",EDGE,"E12.5.1"),sQuery(id+"F1.wireOp",EDGE,"E12.5.2"),sQuery(id+"F1.wireOp",EDGE,"E12.5.3"),sQuery(id+"F1.wireOp",EDGE,"E12.5.4"),sQuery(id+"F1.wireOp",EDGE,"E12.5.5"),sQuery(id+"F1.wireOp",EDGE,"E12.5.6"),sQuery(id+"F1.wireOp",EDGE,"E12.5.7"),sQuery(id+"F1.wireOp",EDGE,"E12.5.8"),sQuery(id+"F1.wireOp",EDGE,"E12.5.9"),sQuery(id+"F1.wireOp",EDGE,"E12.6.0"),sQuery(id+"F1.wireOp",EDGE,"E12.6.1"),sQuery(id+"F1.wireOp",EDGE,"E12.6.2"),sQuery(id+"F1.wireOp",EDGE,"E12.6.3"),sQuery(id+"F1.wireOp",EDGE,"E12.6.4"),sQuery(id+"F1.wireOp",EDGE,"E12.6.5"),sQuery(id+"F1.wireOp",EDGE,"E12.6.6"),sQuery(id+"F1.wireOp",EDGE,"E12.6.7"),sQuery(id+"F1.wireOp",EDGE,"E12.6.8"),sQuery(id+"F1.wireOp",EDGE,"E12.6.9"),sQuery(id+"F1.wireOp",EDGE,"E12.7.0"),sQuery(id+"F1.wireOp",EDGE,"E12.7.1"),sQuery(id+"F1.wireOp",EDGE,"E12.7.2"),sQuery(id+"F1.wireOp",EDGE,"E12.7.3"),sQuery(id+"F1.wireOp",EDGE,"E12.7.4"),sQuery(id+"F1.wireOp",EDGE,"E12.7.5"),sQuery(id+"F1.wireOp",EDGE,"E12.7.6"),sQuery(id+"F1.wireOp",EDGE,"E12.7.7"),sQuery(id+"F1.wireOp",EDGE,"E12.7.8"),sQuery(id+"F1.wireOp",EDGE,"E12.7.9"),sQuery(id+"F1.wireOp",EDGE,"E12.8.0"),sQuery(id+"F1.wireOp",EDGE,"E12.8.1"),sQuery(id+"F1.wireOp",EDGE,"E12.8.2"),sQuery(id+"F1.wireOp",EDGE,"E12.8.3"),sQuery(id+"F1.wireOp",EDGE,"E12.8.4"),sQuery(id+"F1.wireOp",EDGE,"E12.8.5"),sQuery(id+"F1.wireOp",EDGE,"E12.8.6"),sQuery(id+"F1.wireOp",EDGE,"E12.8.7"),sQuery(id+"F1.wireOp",EDGE,"E12.8.8"),sQuery(id+"F1.wireOp",EDGE,"E12.8.9"),sQuery(id+"F1.wireOp",EDGE,"E12.9.0"),sQuery(id+"F1.wireOp",EDGE,"E12.9.1"),sQuery(id+"F1.wireOp",EDGE,"E12.9.2"),sQuery(id+"F1.wireOp",EDGE,"E12.9.3"),sQuery(id+"F1.wireOp",EDGE,"E12.9.4"),sQuery(id+"F1.wireOp",EDGE,"E12.9.5"),sQuery(id+"F1.wireOp",EDGE,"E12.9.6"),sQuery(id+"F1.wireOp",EDGE,"E12.9.7"),sQuery(id+"F1.wireOp",EDGE,"E12.9.8"),sQuery(id+"F1.wireOp",EDGE,"E12.9.9"),sQuery(id+"F1.wireOp",EDGE,"E12.10.0"),sQuery(id+"F1.wireOp",EDGE,"E12.10.1"),sQuery(id+"F1.wireOp",EDGE,"E12.10.2"),sQuery(id+"F1.wireOp",EDGE,"E12.10.3"),sQuery(id+"F1.wireOp",EDGE,"E12.10.4"),sQuery(id+"F1.wireOp",EDGE,"E12.10.5"),sQuery(id+"F1.wireOp",EDGE,"E12.10.6"),sQuery(id+"F1.wireOp",EDGE,"E12.10.7"),sQuery(id+"F1.wireOp",EDGE,"E12.10.8"),sQuery(id+"F1.wireOp",EDGE,"E12.10.9"),sQuery(id+"F1.wireOp",EDGE,"E12.11.0"),sQuery(id+"F1.wireOp",EDGE,"E12.11.1"),sQuery(id+"F1.wireOp",EDGE,"E12.11.2"),sQuery(id+"F1.wireOp",EDGE,"E12.11.3"),sQuery(id+"F1.wireOp",EDGE,"E12.11.4"),sQuery(id+"F1.wireOp",EDGE,"E12.11.5"),sQuery(id+"F1.wireOp",EDGE,"E12.11.6"),sQuery(id+"F1.wireOp",EDGE,"E12.11.7"),sQuery(id+"F1.wireOp",EDGE,"E12.11.8"),sQuery(id+"F1.wireOp",EDGE,"E12.11.9"),sQuery(id+"F1.wireOp",EDGE,"E12.12.0"),sQuery(id+"F1.wireOp",EDGE,"E12.12.1"),sQuery(id+"F1.wireOp",EDGE,"E12.12.2"),sQuery(id+"F1.wireOp",EDGE,"E12.12.3"),sQuery(id+"F1.wireOp",EDGE,"E12.12.4"),sQuery(id+"F1.wireOp",EDGE,"E12.12.5"),sQuery(id+"F1.wireOp",EDGE,"E12.12.6"),sQuery(id+"F1.wireOp",EDGE,"E12.12.7"),sQuery(id+"F1.wireOp",EDGE,"E12.12.8"),sQuery(id+"F1.wireOp",EDGE,"E12.12.9")])],"isStart":false});
            cPlane(context, id + "F6", {"entities" : qUnion([Q0]), "cplaneType" : CPlaneType.OFFSET, "offset" : 3 * mm, "width" : 150 * mm, "height" : 150 * mm});
        }
        {
            var Q0;
            Q0=makeQuery(id+"F2.opExtrude","CAP_FACE",FACE,{"disambiguationData":[OSD([sQuery(id+"F1.wireOp",EDGE,"E0"),sQuery(id+"F1.wireOp",EDGE,"E1"),sQuery(id+"F1.wireOp",EDGE,"E2"),sQuery(id+"F1.wireOp",EDGE,"E5"),sQuery(id+"F1.wireOp",EDGE,"E6"),sQuery(id+"F1.wireOp",EDGE,"E7.MirrorCS"),sQuery(id+"F1.wireOp",EDGE,"E8.MirrorCS"),sQuery(id+"F1.wireOp",EDGE,"E9.MirrorCS"),sQuery(id+"F1.wireOp",EDGE,"E10.MirrorCS"),sQuery(id+"F1.wireOp",EDGE,"E11"),sQuery(id+"F1.wireOp",EDGE,"E12.1.0"),sQuery(id+"F1.wireOp",EDGE,"E12.1.1"),sQuery(id+"F1.wireOp",EDGE,"E12.1.2"),sQuery(id+"F1.wireOp",EDGE,"E12.1.3"),sQuery(id+"F1.wireOp",EDGE,"E12.1.4"),sQuery(id+"F1.wireOp",EDGE,"E12.1.5"),sQuery(id+"F1.wireOp",EDGE,"E12.1.6"),sQuery(id+"F1.wireOp",EDGE,"E12.1.7"),sQuery(id+"F1.wireOp",EDGE,"E12.1.8"),sQuery(id+"F1.wireOp",EDGE,"E12.1.9"),sQuery(id+"F1.wireOp",EDGE,"E12.2.0"),sQuery(id+"F1.wireOp",EDGE,"E12.2.1"),sQuery(id+"F1.wireOp",EDGE,"E12.2.2"),sQuery(id+"F1.wireOp",EDGE,"E12.2.3"),sQuery(id+"F1.wireOp",EDGE,"E12.2.4"),sQuery(id+"F1.wireOp",EDGE,"E12.2.5"),sQuery(id+"F1.wireOp",EDGE,"E12.2.6"),sQuery(id+"F1.wireOp",EDGE,"E12.2.7"),sQuery(id+"F1.wireOp",EDGE,"E12.2.8"),sQuery(id+"F1.wireOp",EDGE,"E12.2.9"),sQuery(id+"F1.wireOp",EDGE,"E12.3.0"),sQuery(id+"F1.wireOp",EDGE,"E12.3.1"),sQuery(id+"F1.wireOp",EDGE,"E12.3.2"),sQuery(id+"F1.wireOp",EDGE,"E12.3.3"),sQuery(id+"F1.wireOp",EDGE,"E12.3.4"),sQuery(id+"F1.wireOp",EDGE,"E12.3.5"),sQuery(id+"F1.wireOp",EDGE,"E12.3.6"),sQuery(id+"F1.wireOp",EDGE,"E12.3.7"),sQuery(id+"F1.wireOp",EDGE,"E12.3.8"),sQuery(id+"F1.wireOp",EDGE,"E12.3.9"),sQuery(id+"F1.wireOp",EDGE,"E12.4.0"),sQuery(id+"F1.wireOp",EDGE,"E12.4.1"),sQuery(id+"F1.wireOp",EDGE,"E12.4.2"),sQuery(id+"F1.wireOp",EDGE,"E12.4.3"),sQuery(id+"F1.wireOp",EDGE,"E12.4.4"),sQuery(id+"F1.wireOp",EDGE,"E12.4.5"),sQuery(id+"F1.wireOp",EDGE,"E12.4.6"),sQuery(id+"F1.wireOp",EDGE,"E12.4.7"),sQuery(id+"F1.wireOp",EDGE,"E12.4.8"),sQuery(id+"F1.wireOp",EDGE,"E12.4.9"),sQuery(id+"F1.wireOp",EDGE,"E12.5.0"),sQuery(id+"F1.wireOp",EDGE,"E12.5.1"),sQuery(id+"F1.wireOp",EDGE,"E12.5.2"),sQuery(id+"F1.wireOp",EDGE,"E12.5.3"),sQuery(id+"F1.wireOp",EDGE,"E12.5.4"),sQuery(id+"F1.wireOp",EDGE,"E12.5.5"),sQuery(id+"F1.wireOp",EDGE,"E12.5.6"),sQuery(id+"F1.wireOp",EDGE,"E12.5.7"),sQuery(id+"F1.wireOp",EDGE,"E12.5.8"),sQuery(id+"F1.wireOp",EDGE,"E12.5.9"),sQuery(id+"F1.wireOp",EDGE,"E12.6.0"),sQuery(id+"F1.wireOp",EDGE,"E12.6.1"),sQuery(id+"F1.wireOp",EDGE,"E12.6.2"),sQuery(id+"F1.wireOp",EDGE,"E12.6.3"),sQuery(id+"F1.wireOp",EDGE,"E12.6.4"),sQuery(id+"F1.wireOp",EDGE,"E12.6.5"),sQuery(id+"F1.wireOp",EDGE,"E12.6.6"),sQuery(id+"F1.wireOp",EDGE,"E12.6.7"),sQuery(id+"F1.wireOp",EDGE,"E12.6.8"),sQuery(id+"F1.wireOp",EDGE,"E12.6.9"),sQuery(id+"F1.wireOp",EDGE,"E12.7.0"),sQuery(id+"F1.wireOp",EDGE,"E12.7.1"),sQuery(id+"F1.wireOp",EDGE,"E12.7.2"),sQuery(id+"F1.wireOp",EDGE,"E12.7.3"),sQuery(id+"F1.wireOp",EDGE,"E12.7.4"),sQuery(id+"F1.wireOp",EDGE,"E12.7.5"),sQuery(id+"F1.wireOp",EDGE,"E12.7.6"),sQuery(id+"F1.wireOp",EDGE,"E12.7.7"),sQuery(id+"F1.wireOp",EDGE,"E12.7.8"),sQuery(id+"F1.wireOp",EDGE,"E12.7.9"),sQuery(id+"F1.wireOp",EDGE,"E12.8.0"),sQuery(id+"F1.wireOp",EDGE,"E12.8.1"),sQuery(id+"F1.wireOp",EDGE,"E12.8.2"),sQuery(id+"F1.wireOp",EDGE,"E12.8.3"),sQuery(id+"F1.wireOp",EDGE,"E12.8.4"),sQuery(id+"F1.wireOp",EDGE,"E12.8.5"),sQuery(id+"F1.wireOp",EDGE,"E12.8.6"),sQuery(id+"F1.wireOp",EDGE,"E12.8.7"),sQuery(id+"F1.wireOp",EDGE,"E12.8.8"),sQuery(id+"F1.wireOp",EDGE,"E12.8.9"),sQuery(id+"F1.wireOp",EDGE,"E12.9.0"),sQuery(id+"F1.wireOp",EDGE,"E12.9.1"),sQuery(id+"F1.wireOp",EDGE,"E12.9.2"),sQuery(id+"F1.wireOp",EDGE,"E12.9.3"),sQuery(id+"F1.wireOp",EDGE,"E12.9.4"),sQuery(id+"F1.wireOp",EDGE,"E12.9.5"),sQuery(id+"F1.wireOp",EDGE,"E12.9.6"),sQuery(id+"F1.wireOp",EDGE,"E12.9.7"),sQuery(id+"F1.wireOp",EDGE,"E12.9.8"),sQuery(id+"F1.wireOp",EDGE,"E12.9.9"),sQuery(id+"F1.wireOp",EDGE,"E12.10.0"),sQuery(id+"F1.wireOp",EDGE,"E12.10.1"),sQuery(id+"F1.wireOp",EDGE,"E12.10.2"),sQuery(id+"F1.wireOp",EDGE,"E12.10.3"),sQuery(id+"F1.wireOp",EDGE,"E12.10.4"),sQuery(id+"F1.wireOp",EDGE,"E12.10.5"),sQuery(id+"F1.wireOp",EDGE,"E12.10.6"),sQuery(id+"F1.wireOp",EDGE,"E12.10.7"),sQuery(id+"F1.wireOp",EDGE,"E12.10.8"),sQuery(id+"F1.wireOp",EDGE,"E12.10.9"),sQuery(id+"F1.wireOp",EDGE,"E12.11.0"),sQuery(id+"F1.wireOp",EDGE,"E12.11.1"),sQuery(id+"F1.wireOp",EDGE,"E12.11.2"),sQuery(id+"F1.wireOp",EDGE,"E12.11.3"),sQuery(id+"F1.wireOp",EDGE,"E12.11.4"),sQuery(id+"F1.wireOp",EDGE,"E12.11.5"),sQuery(id+"F1.wireOp",EDGE,"E12.11.6"),sQuery(id+"F1.wireOp",EDGE,"E12.11.7"),sQuery(id+"F1.wireOp",EDGE,"E12.11.8"),sQuery(id+"F1.wireOp",EDGE,"E12.11.9"),sQuery(id+"F1.wireOp",EDGE,"E12.12.0"),sQuery(id+"F1.wireOp",EDGE,"E12.12.1"),sQuery(id+"F1.wireOp",EDGE,"E12.12.2"),sQuery(id+"F1.wireOp",EDGE,"E12.12.3"),sQuery(id+"F1.wireOp",EDGE,"E12.12.4"),sQuery(id+"F1.wireOp",EDGE,"E12.12.5"),sQuery(id+"F1.wireOp",EDGE,"E12.12.6"),sQuery(id+"F1.wireOp",EDGE,"E12.12.7"),sQuery(id+"F1.wireOp",EDGE,"E12.12.8"),sQuery(id+"F1.wireOp",EDGE,"E12.12.9")])],"isStart":false});
            var sketch = newSketch(context, id + "F7", { "sketchPlane" : qUnion([Q0])});
            skCircle(sketch, "E15", {"center": v(0, 0) * mm, "radius": 8 * mm});
            skSolve(sketch);
        }
        {
            var Q0;
            Q0=qCreatedBy(id+"F6.planeOp",FACE);
            var sketch = newSketch(context, id + "F8", { "sketchPlane" : qUnion([Q0])});
            skCircle(sketch, "E16", {"center": v(0, 0) * mm, "radius": 11.08 * mm});
            skSolve(sketch);
        }
        {
            var Q0;
            Q0 = qSketchRegion(id + "F7", true);
            var Q1;
            Q1 = qSketchRegion(id + "F8", true);
            loft(context, id + "F9", {"sheetProfilesArray" : [{ "sheetProfileEntities" : qUnion([Q0]) }, { "sheetProfileEntities" : qUnion([Q1]) }]});
        }
        {
            var Q0;
            Q0=makeQuery(id+"F9.opLoft","CAP_FACE",FACE,{"disambiguationData":[OSD([makeQuery(id+"F8.imprint","IMPRINT",FACE,{"disambiguationData":[TD([[makeQuery(id+"F8.imprint","IMPRINT",EDGE,{"derivedFrom":sQuery(id+"F8.wireOp",EDGE,"E16")}),1.0]])]})])],"isStart":true});
            var sketch = newSketch(context, id + "F10", { "sketchPlane" : qUnion([Q0])});
            skCircle(sketch, "E17.0.0", {"center": v(0, 0) * mm, "radius": 11.08 * mm});
            skSolve(sketch);
        }
        {
            var Q0;
            Q0 = qSketchRegion(id + "F10", true);
            extrude(context, id + "F11", {"entities" : qUnion([Q0]), "operationType" : NewBodyOperationType.ADD, "depth" : 9 * mm});
        }
        {
            var Q0;
            Q0=makeQuery(id+"F11.opExtrude","CAP_FACE",FACE,{"disambiguationData":[OSD([sQuery(id+"F10.wireOp",EDGE,"E17.0.0")])],"isStart":false});
            var sketch = newSketch(context, id + "F12", { "sketchPlane" : qUnion([Q0])});
            skCircle(sketch, "E18", {"center": v(0, 0) * mm, "radius": 3.15 * mm});
            skSolve(sketch);
        }
        {
            var Q0;
            Q0 = qSketchRegion(id + "F12", true);
            var Q1;
            Q1=makeQuery(id+"F5.opPattern","COPY",FACE,{"derivedFrom":makeQuery(id+"F2.opExtrude","CAP_FACE",FACE,{"disambiguationData":[OSD([sQuery(id+"F1.wireOp",EDGE,"E0"),sQuery(id+"F1.wireOp",EDGE,"E1"),sQuery(id+"F1.wireOp",EDGE,"E2"),sQuery(id+"F1.wireOp",EDGE,"E5"),sQuery(id+"F1.wireOp",EDGE,"E6"),sQuery(id+"F1.wireOp",EDGE,"E7.MirrorCS"),sQuery(id+"F1.wireOp",EDGE,"E8.MirrorCS"),sQuery(id+"F1.wireOp",EDGE,"E9.MirrorCS"),sQuery(id+"F1.wireOp",EDGE,"E10.MirrorCS"),sQuery(id+"F1.wireOp",EDGE,"E11"),sQuery(id+"F1.wireOp",EDGE,"E12.1.0"),sQuery(id+"F1.wireOp",EDGE,"E12.1.1"),sQuery(id+"F1.wireOp",EDGE,"E12.1.2"),sQuery(id+"F1.wireOp",EDGE,"E12.1.3"),sQuery(id+"F1.wireOp",EDGE,"E12.1.4"),sQuery(id+"F1.wireOp",EDGE,"E12.1.5"),sQuery(id+"F1.wireOp",EDGE,"E12.1.6"),sQuery(id+"F1.wireOp",EDGE,"E12.1.7"),sQuery(id+"F1.wireOp",EDGE,"E12.1.8"),sQuery(id+"F1.wireOp",EDGE,"E12.1.9"),sQuery(id+"F1.wireOp",EDGE,"E12.2.0"),sQuery(id+"F1.wireOp",EDGE,"E12.2.1"),sQuery(id+"F1.wireOp",EDGE,"E12.2.2"),sQuery(id+"F1.wireOp",EDGE,"E12.2.3"),sQuery(id+"F1.wireOp",EDGE,"E12.2.4"),sQuery(id+"F1.wireOp",EDGE,"E12.2.5"),sQuery(id+"F1.wireOp",EDGE,"E12.2.6"),sQuery(id+"F1.wireOp",EDGE,"E12.2.7"),sQuery(id+"F1.wireOp",EDGE,"E12.2.8"),sQuery(id+"F1.wireOp",EDGE,"E12.2.9"),sQuery(id+"F1.wireOp",EDGE,"E12.3.0"),sQuery(id+"F1.wireOp",EDGE,"E12.3.1"),sQuery(id+"F1.wireOp",EDGE,"E12.3.2"),sQuery(id+"F1.wireOp",EDGE,"E12.3.3"),sQuery(id+"F1.wireOp",EDGE,"E12.3.4"),sQuery(id+"F1.wireOp",EDGE,"E12.3.5"),sQuery(id+"F1.wireOp",EDGE,"E12.3.6"),sQuery(id+"F1.wireOp",EDGE,"E12.3.7"),sQuery(id+"F1.wireOp",EDGE,"E12.3.8"),sQuery(id+"F1.wireOp",EDGE,"E12.3.9"),sQuery(id+"F1.wireOp",EDGE,"E12.4.0"),sQuery(id+"F1.wireOp",EDGE,"E12.4.1"),sQuery(id+"F1.wireOp",EDGE,"E12.4.2"),sQuery(id+"F1.wireOp",EDGE,"E12.4.3"),sQuery(id+"F1.wireOp",EDGE,"E12.4.4"),sQuery(id+"F1.wireOp",EDGE,"E12.4.5"),sQuery(id+"F1.wireOp",EDGE,"E12.4.6"),sQuery(id+"F1.wireOp",EDGE,"E12.4.7"),sQuery(id+"F1.wireOp",EDGE,"E12.4.8"),sQuery(id+"F1.wireOp",EDGE,"E12.4.9"),sQuery(id+"F1.wireOp",EDGE,"E12.5.0"),sQuery(id+"F1.wireOp",EDGE,"E12.5.1"),sQuery(id+"F1.wireOp",EDGE,"E12.5.2"),sQuery(id+"F1.wireOp",EDGE,"E12.5.3"),sQuery(id+"F1.wireOp",EDGE,"E12.5.4"),sQuery(id+"F1.wireOp",EDGE,"E12.5.5"),sQuery(id+"F1.wireOp",EDGE,"E12.5.6"),sQuery(id+"F1.wireOp",EDGE,"E12.5.7"),sQuery(id+"F1.wireOp",EDGE,"E12.5.8"),sQuery(id+"F1.wireOp",EDGE,"E12.5.9"),sQuery(id+"F1.wireOp",EDGE,"E12.6.0"),sQuery(id+"F1.wireOp",EDGE,"E12.6.1"),sQuery(id+"F1.wireOp",EDGE,"E12.6.2"),sQuery(id+"F1.wireOp",EDGE,"E12.6.3"),sQuery(id+"F1.wireOp",EDGE,"E12.6.4"),sQuery(id+"F1.wireOp",EDGE,"E12.6.5"),sQuery(id+"F1.wireOp",EDGE,"E12.6.6"),sQuery(id+"F1.wireOp",EDGE,"E12.6.7"),sQuery(id+"F1.wireOp",EDGE,"E12.6.8"),sQuery(id+"F1.wireOp",EDGE,"E12.6.9"),sQuery(id+"F1.wireOp",EDGE,"E12.7.0"),sQuery(id+"F1.wireOp",EDGE,"E12.7.1"),sQuery(id+"F1.wireOp",EDGE,"E12.7.2"),sQuery(id+"F1.wireOp",EDGE,"E12.7.3"),sQuery(id+"F1.wireOp",EDGE,"E12.7.4"),sQuery(id+"F1.wireOp",EDGE,"E12.7.5"),sQuery(id+"F1.wireOp",EDGE,"E12.7.6"),sQuery(id+"F1.wireOp",EDGE,"E12.7.7"),sQuery(id+"F1.wireOp",EDGE,"E12.7.8"),sQuery(id+"F1.wireOp",EDGE,"E12.7.9"),sQuery(id+"F1.wireOp",EDGE,"E12.8.0"),sQuery(id+"F1.wireOp",EDGE,"E12.8.1"),sQuery(id+"F1.wireOp",EDGE,"E12.8.2"),sQuery(id+"F1.wireOp",EDGE,"E12.8.3"),sQuery(id+"F1.wireOp",EDGE,"E12.8.4"),sQuery(id+"F1.wireOp",EDGE,"E12.8.5"),sQuery(id+"F1.wireOp",EDGE,"E12.8.6"),sQuery(id+"F1.wireOp",EDGE,"E12.8.7"),sQuery(id+"F1.wireOp",EDGE,"E12.8.8"),sQuery(id+"F1.wireOp",EDGE,"E12.8.9"),sQuery(id+"F1.wireOp",EDGE,"E12.9.0"),sQuery(id+"F1.wireOp",EDGE,"E12.9.1"),sQuery(id+"F1.wireOp",EDGE,"E12.9.2"),sQuery(id+"F1.wireOp",EDGE,"E12.9.3"),sQuery(id+"F1.wireOp",EDGE,"E12.9.4"),sQuery(id+"F1.wireOp",EDGE,"E12.9.5"),sQuery(id+"F1.wireOp",EDGE,"E12.9.6"),sQuery(id+"F1.wireOp",EDGE,"E12.9.7"),sQuery(id+"F1.wireOp",EDGE,"E12.9.8"),sQuery(id+"F1.wireOp",EDGE,"E12.9.9"),sQuery(id+"F1.wireOp",EDGE,"E12.10.0"),sQuery(id+"F1.wireOp",EDGE,"E12.10.1"),sQuery(id+"F1.wireOp",EDGE,"E12.10.2"),sQuery(id+"F1.wireOp",EDGE,"E12.10.3"),sQuery(id+"F1.wireOp",EDGE,"E12.10.4"),sQuery(id+"F1.wireOp",EDGE,"E12.10.5"),sQuery(id+"F1.wireOp",EDGE,"E12.10.6"),sQuery(id+"F1.wireOp",EDGE,"E12.10.7"),sQuery(id+"F1.wireOp",EDGE,"E12.10.8"),sQuery(id+"F1.wireOp",EDGE,"E12.10.9"),sQuery(id+"F1.wireOp",EDGE,"E12.11.0"),sQuery(id+"F1.wireOp",EDGE,"E12.11.1"),sQuery(id+"F1.wireOp",EDGE,"E12.11.2"),sQuery(id+"F1.wireOp",EDGE,"E12.11.3"),sQuery(id+"F1.wireOp",EDGE,"E12.11.4"),sQuery(id+"F1.wireOp",EDGE,"E12.11.5"),sQuery(id+"F1.wireOp",EDGE,"E12.11.6"),sQuery(id+"F1.wireOp",EDGE,"E12.11.7"),sQuery(id+"F1.wireOp",EDGE,"E12.11.8"),sQuery(id+"F1.wireOp",EDGE,"E12.11.9"),sQuery(id+"F1.wireOp",EDGE,"E12.12.0"),sQuery(id+"F1.wireOp",EDGE,"E12.12.1"),sQuery(id+"F1.wireOp",EDGE,"E12.12.2"),sQuery(id+"F1.wireOp",EDGE,"E12.12.3"),sQuery(id+"F1.wireOp",EDGE,"E12.12.4"),sQuery(id+"F1.wireOp",EDGE,"E12.12.5"),sQuery(id+"F1.wireOp",EDGE,"E12.12.6"),sQuery(id+"F1.wireOp",EDGE,"E12.12.7"),sQuery(id+"F1.wireOp",EDGE,"E12.12.8"),sQuery(id+"F1.wireOp",EDGE,"E12.12.9")])],"isStart":false}),"instanceName":"1"});
            extrude(context, id + "F13", {"entities" : qUnion([Q0]), "operationType" : NewBodyOperationType.REMOVE, "endBound" : BoundingType.UP_TO_SURFACE, "oppositeDirection" : true, "endBoundEntityFace" : qUnion([Q1]), "depth" : 25 * mm});
        }
        {
            var Q0;
            Q0=makeQuery(id+"F11.opExtrude","CAP_FACE",FACE,{"disambiguationData":[OSD([sQuery(id+"F10.wireOp",EDGE,"E17.0.0")])],"isStart":false});
            var sketch = newSketch(context, id + "F14", { "sketchPlane" : qUnion([Q0])});
            skLineSegment(sketch, "E19.bottom", {"start": v(-3.25, 7.98) * mm, "end": v(3.25, 7.98) * mm});
            skLineSegment(sketch, "E19.top", {"start": v(-3.25, 5.23) * mm, "end": v(3.25, 5.23) * mm});
            skLineSegment(sketch, "E19.left", {"start": v(-3.25, 7.98) * mm, "end": v(-3.25, 5.23) * mm});
            skLineSegment(sketch, "E19.right", {"start": v(3.25, 7.98) * mm, "end": v(3.25, 5.23) * mm});
            skLineSegment(sketch, "E20", {"start": v(0, 0) * mm, "end": v(0, 9.89) * mm, "construction": true});
            skSolve(sketch);
        }
        {
            var Q0;
            Q0 = qSketchRegion(id + "F14", true);
            extrude(context, id + "F15", {"entities" : qUnion([Q0]), "operationType" : NewBodyOperationType.REMOVE, "oppositeDirection" : true, "depth" : 9 * mm});
        }
        {
            var Q0;
            Q0=makeQuery(id+"F15.boolean.opBoolean","COPY",FACE,{"derivedFrom":makeQuery(id+"F15.opExtrude","SWEPT_FACE",FACE,{"disambiguationData":[OSD([sQuery(id+"F14.wireOp",EDGE,"E19.bottom")])]})});
            var sketch = newSketch(context, id + "F16", { "sketchPlane" : qUnion([Q0])});
            skLineSegment(sketch, "E21", {"start": v(0, -3.01) * mm, "end": v(0, -12.01) * mm, "construction": true});
            skLineSegment(sketch, "E22", {"start": v(-3.25, -7.51) * mm, "end": v(3.25, -7.51) * mm, "construction": true});
            skCircle(sketch, "E23", {"center": v(0, -7.51) * mm, "radius": 1.63 * mm});
            skSolve(sketch);
        }
        {
            var Q0;
            Q0 = qSketchRegion(id + "F16", true);
            extrude(context, id + "F17", {"entities" : qUnion([Q0]), "operationType" : NewBodyOperationType.REMOVE, "endBound" : BoundingType.SYMMETRIC, "oppositeDirection" : true, "depth" : 12 * mm});
        }
    });
